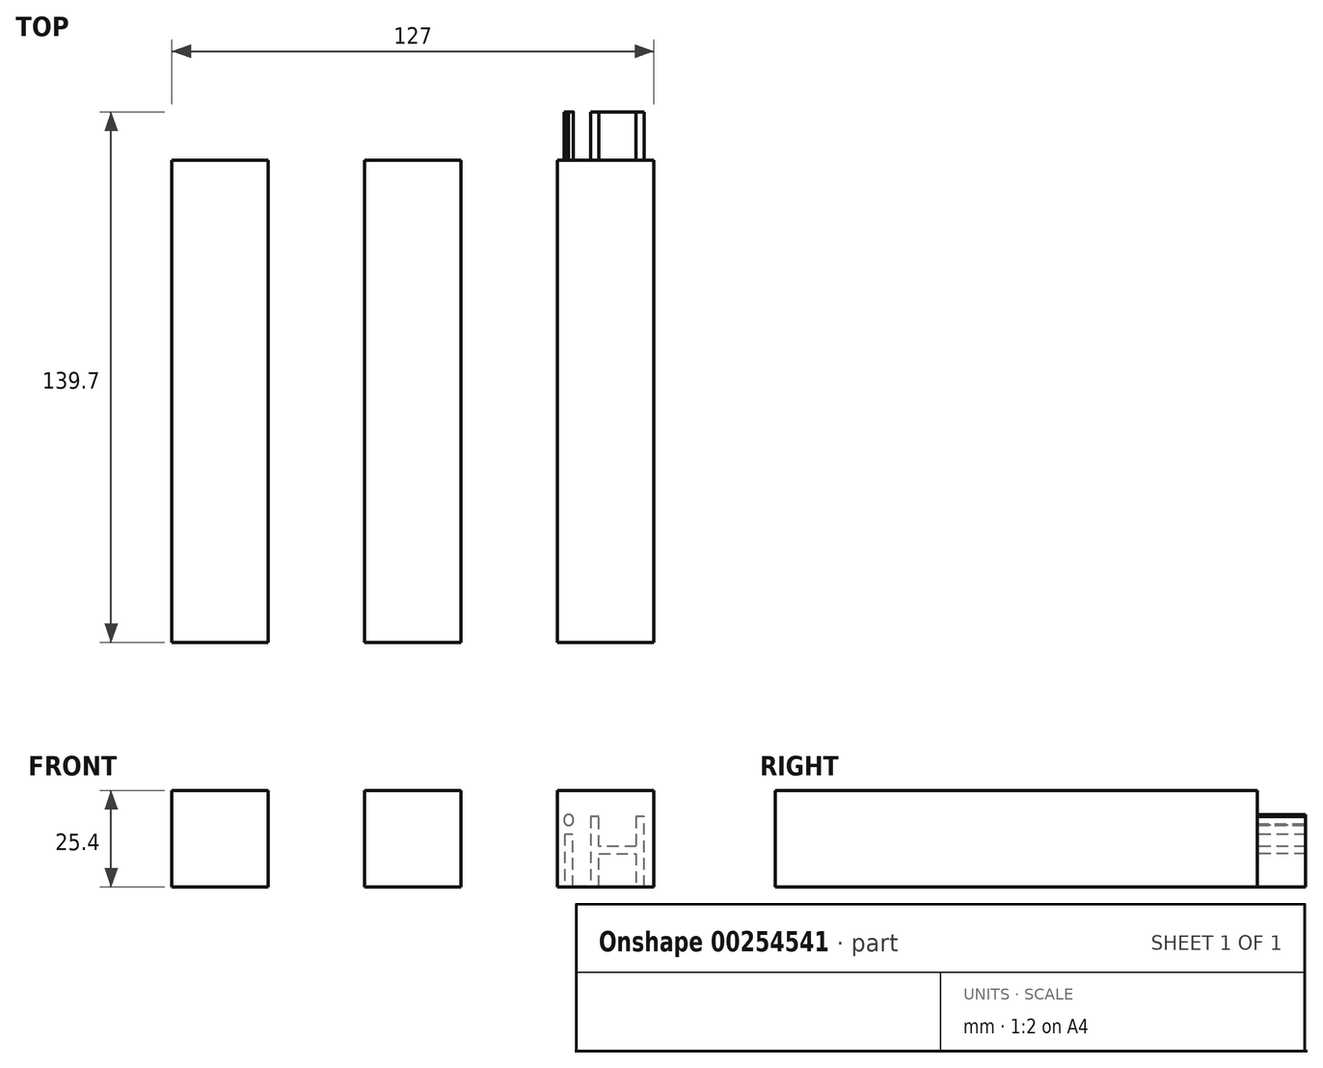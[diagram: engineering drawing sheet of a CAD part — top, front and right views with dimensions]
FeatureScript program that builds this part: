
annotation { "Feature Type Name" : "Feature", "Feature Type Description" : "" }
export const myFeature = defineFeature(function(context is Context, id is Id, definition is map)
    precondition{}
    {
        {
            var Q0;
            Q0=qCreatedBy(makeId("Front.planeOp"),FACE);
            var sketch = newSketch(context, id + "F0", { "sketchPlane" : qUnion([Q0])});
            skLineSegment(sketch, "E0.bottom", {"start": v(12.7, 12.7) * mm, "end": v(-12.7, 12.7) * mm});
            skLineSegment(sketch, "E0.top", {"start": v(12.7, -12.7) * mm, "end": v(-12.7, -12.7) * mm});
            skLineSegment(sketch, "E0.left", {"start": v(12.7, 12.7) * mm, "end": v(12.7, -12.7) * mm});
            skLineSegment(sketch, "E0.right", {"start": v(-12.7, 12.7) * mm, "end": v(-12.7, -12.7) * mm});
            skPoint(sketch, "E0.middle", {"position": v(0, 0) * mm});
            skPoint(sketch, "E1.endSnap0", {"position": v(12.7, 0) * mm});
            skLineSegment(sketch, "E2.bottom", {"start": v(63.5, 12.7) * mm, "end": v(38.1, 12.7) * mm});
            skLineSegment(sketch, "E2.top", {"start": v(63.5, -12.7) * mm, "end": v(38.1, -12.7) * mm});
            skLineSegment(sketch, "E2.left", {"start": v(63.5, 12.7) * mm, "end": v(63.5, -12.7) * mm});
            skLineSegment(sketch, "E2.right", {"start": v(38.1, 12.7) * mm, "end": v(38.1, -12.7) * mm});
            skPoint(sketch, "E2.middle", {"position": v(50.8, 0) * mm});
            skLineSegment(sketch, "E3.bottom", {"start": v(-38.1, 12.7) * mm, "end": v(-63.5, 12.7) * mm});
            skLineSegment(sketch, "E3.top", {"start": v(-38.1, -12.7) * mm, "end": v(-63.5, -12.7) * mm});
            skLineSegment(sketch, "E3.left", {"start": v(-38.1, 12.7) * mm, "end": v(-38.1, -12.7) * mm});
            skLineSegment(sketch, "E3.right", {"start": v(-63.5, 12.7) * mm, "end": v(-63.5, -12.7) * mm});
            skPoint(sketch, "E3.middle", {"position": v(-50.8, 0) * mm});
            skSolve(sketch);
        }
        {
            var Q0;
            Q0=makeQuery(id+"F0.imprint","IMPRINT",FACE,{"disambiguationData":[TD([[makeQuery(id+"F0.imprint","IMPRINT",EDGE,{"derivedFrom":sQuery(id+"F0.wireOp",EDGE,"E2.bottom")}),1.0]])]});
            var Q1;
            Q1=makeQuery(id+"F0.imprint","IMPRINT",FACE,{"disambiguationData":[TD([[makeQuery(id+"F0.imprint","IMPRINT",EDGE,{"derivedFrom":sQuery(id+"F0.wireOp",EDGE,"E0.bottom")}),1.0]])]});
            var Q2;
            Q2=makeQuery(id+"F0.imprint","IMPRINT",FACE,{"disambiguationData":[TD([[makeQuery(id+"F0.imprint","IMPRINT",EDGE,{"derivedFrom":sQuery(id+"F0.wireOp",EDGE,"E3.bottom")}),1.0]])]});
            extrude(context, id + "F1", {"entities" : qUnion([Q0, Q1, Q2]), "endBound" : BoundingType.SYMMETRIC, "depth" : 127 * mm});
        }
        {
            var Q0;
            Q0=makeQuery(id+"F1.opExtrude","CAP_FACE",FACE,{"disambiguationData":[OSD([sQuery(id+"F0.wireOp",EDGE,"E2.bottom"),sQuery(id+"F0.wireOp",EDGE,"E2.top"),sQuery(id+"F0.wireOp",EDGE,"E2.left"),sQuery(id+"F0.wireOp",EDGE,"E2.right")])],"isStart":true});
            var sketch = newSketch(context, id + "F2", { "sketchPlane" : qUnion([Q0])});
            skText(sketch, "E4", { "text": "Hi", "fontName": "OpenSans-Regular.ttf"});
            const initialGuessF2  = {"E4": [-0.0635, -0.0127, 1, 0, 0.0187]};
            skSetInitialGuess(sketch, initialGuessF2);
            skSolve(sketch);
        }
        {
            var Q0;
            Q0 = qSketchRegion(id + "F2", true);
            extrude(context, id + "F3", {"entities" : qUnion([Q0]), "operationType" : NewBodyOperationType.ADD, "depth" : 12.7 * mm});
        }
    });
